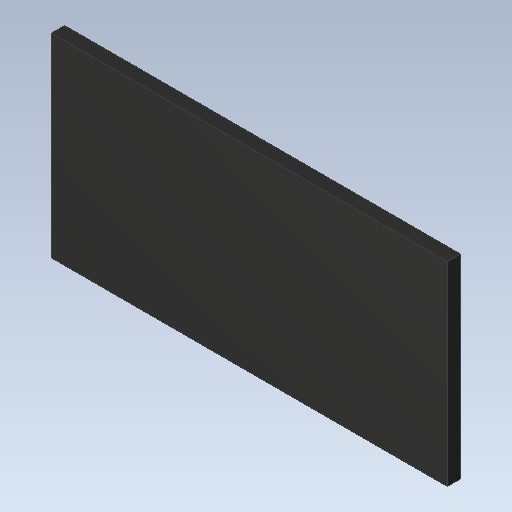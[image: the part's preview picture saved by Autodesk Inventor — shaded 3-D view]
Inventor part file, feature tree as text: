
AUTODESK INVENTOR PART (.ipt)
format: ipt  version: 2020 (Build 240168000, 168)  size: 87,040 bytes
history: imported  units: in
note: dims shown in document units (in); Inventor stores cm internally (conversion verified against a paired STEP export)
features: imported_body x1
ambient origin geometry x8: Origin, YZ Plane, XZ Plane, XY Plane, X Axis, Y Axis, Z Axis, Center Point
bodies: Solid1 (imported_parasolid), Body1 (imported_parasolid)
feature tree (1):
  imported_body  NMx_Import_Brep_tag  [imported B-rep: ~6 faces, bbox_mm=[2.9972, 1.4732, 0.1]]
